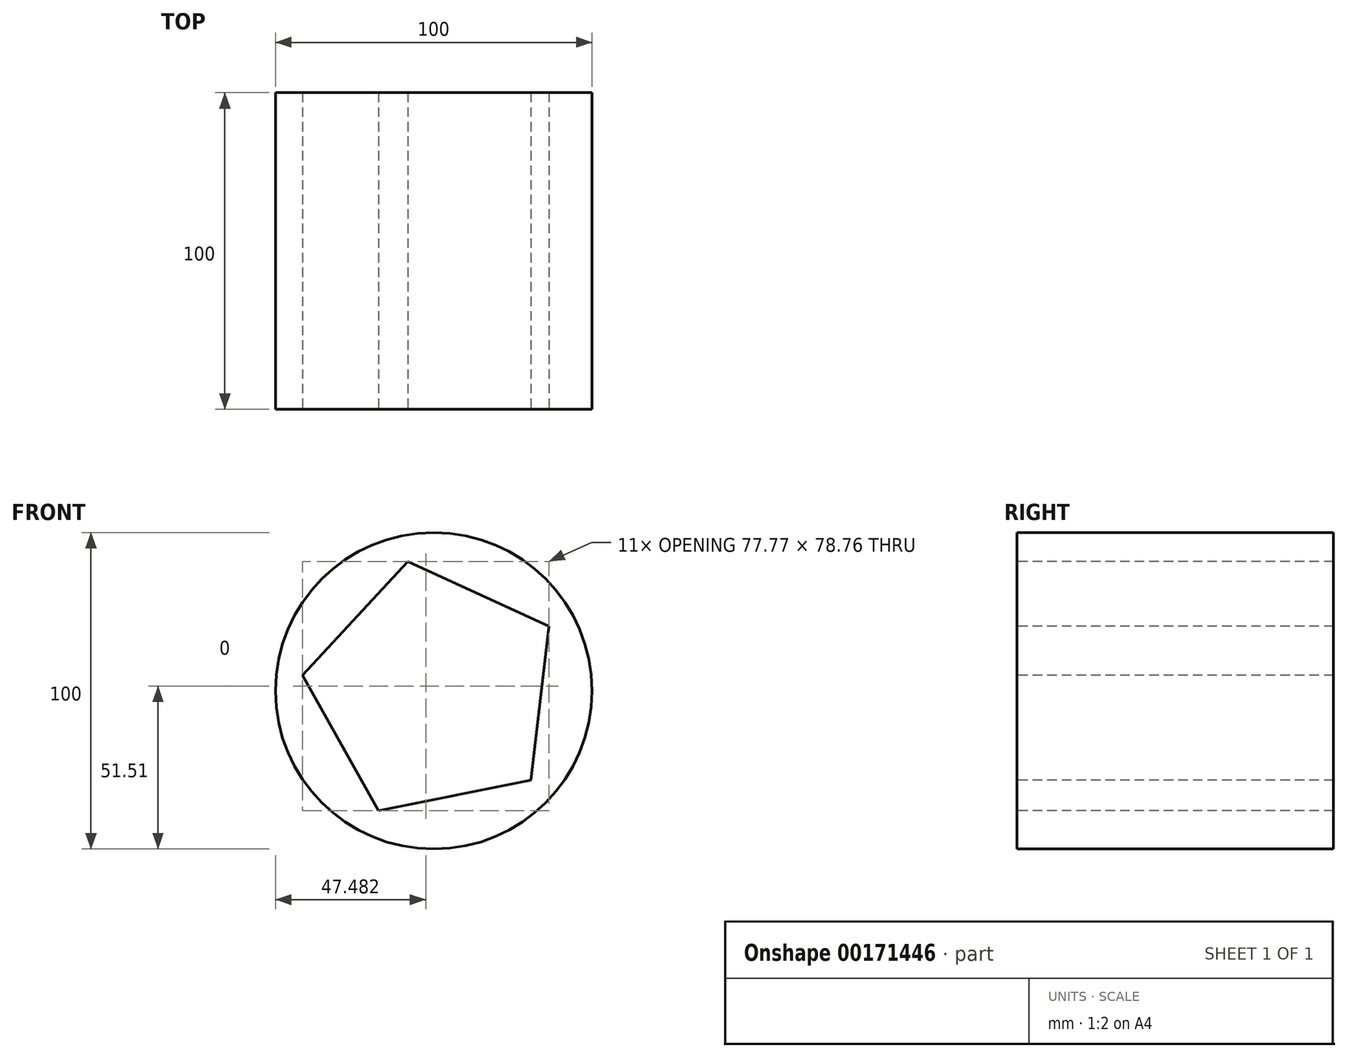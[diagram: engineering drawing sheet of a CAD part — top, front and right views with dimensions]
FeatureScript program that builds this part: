
annotation { "Feature Type Name" : "Feature", "Feature Type Description" : "" }
export const myFeature = defineFeature(function(context is Context, id is Id, definition is map)
    precondition{}
    {
        {
            var Q0;
            Q0=qCreatedBy(makeId("Front.planeOp"),FACE);
            var sketch = newSketch(context, id + "F0", { "sketchPlane" : qUnion([Q0])});
            skCircle(sketch, "E0", {"center": v(0, 0) * mm, "radius": 50 * mm});
            skSolve(sketch);
        }
        {
            var Q0;
            Q0=makeQuery(id+"F0.imprint","IMPRINT",FACE,{"disambiguationData":[TD([[makeQuery(id+"F0.imprint","IMPRINT",EDGE,{"derivedFrom":sQuery(id+"F0.wireOp",EDGE,"E0")}),1.0]])]});
            extrude(context, id + "F1", {"entities" : qUnion([Q0]), "endBound" : BoundingType.SYMMETRIC, "depth" : 100 * mm});
        }
        {
            var Q0;
            Q0=makeQuery(id+"F1.opExtrude","CAP_FACE",FACE,{"disambiguationData":[OSD([sQuery(id+"F0.wireOp",EDGE,"E0")])],"isStart":false});
            var sketch = newSketch(context, id + "F2", { "sketchPlane" : qUnion([Q0])});
            skCircle(sketch, "E1.cCircle", {"center": v(0, 0) * mm, "radius": 41.7 * mm, "construction": true});
            skLineSegment(sketch, "E1.0", {"start": v(36.37, 20.38) * mm, "end": v(30.62, -28.29) * mm});
            skLineSegment(sketch, "E1.1", {"start": v(30.62, -28.29) * mm, "end": v(-17.44, -37.87) * mm});
            skLineSegment(sketch, "E1.2", {"start": v(-17.44, -37.87) * mm, "end": v(-41.4, 4.89) * mm});
            skLineSegment(sketch, "E1.3", {"start": v(-41.4, 4.89) * mm, "end": v(-8.15, 40.89) * mm});
            skLineSegment(sketch, "E1.4", {"start": v(-8.15, 40.89) * mm, "end": v(36.37, 20.38) * mm});
            skSolve(sketch);
        }
        {
            var Q0;
            Q0=makeQuery(id+"F2.imprint","IMPRINT",FACE,{"disambiguationData":[TD([[makeQuery(id+"F2.imprint","IMPRINT",EDGE,{"derivedFrom":sQuery(id+"F2.wireOp",EDGE,"E1.0")}),-1.0]])]});
            extrude(context, id + "F3", {"entities" : qUnion([Q0]), "operationType" : NewBodyOperationType.REMOVE, "oppositeDirection" : true, "depth" : 100 * mm});
        }
    });
